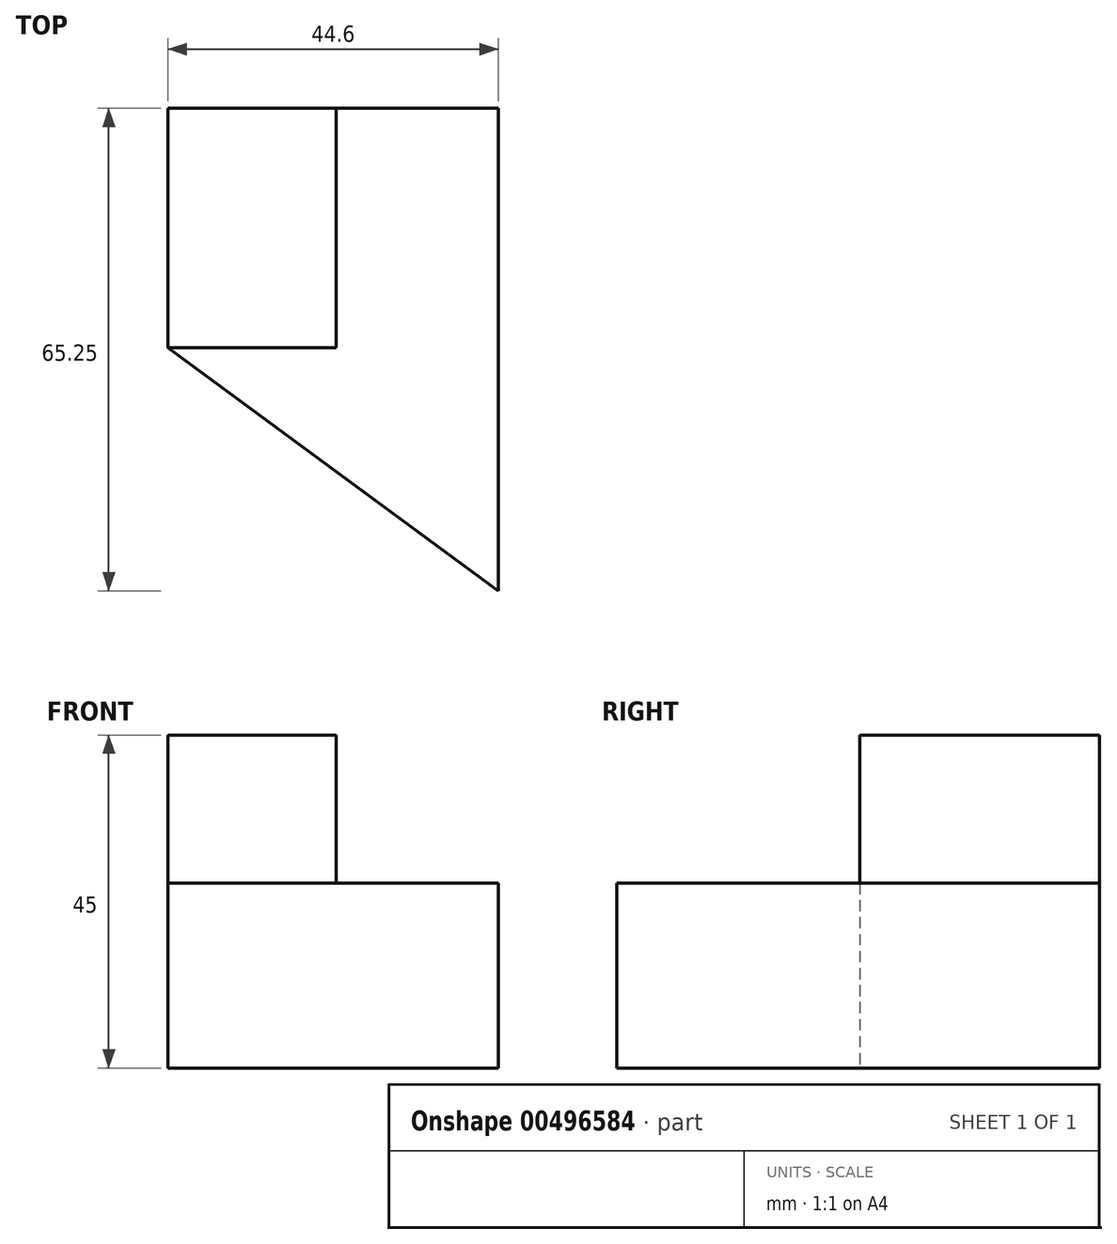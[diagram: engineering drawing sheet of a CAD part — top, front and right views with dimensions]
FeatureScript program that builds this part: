
annotation { "Feature Type Name" : "Feature", "Feature Type Description" : "" }
export const myFeature = defineFeature(function(context is Context, id is Id, definition is map)
    precondition{}
    {
        {
            var Q0;
            Q0=qCreatedBy(makeId("Top.planeOp"),FACE);
            var sketch = newSketch(context, id + "F0", { "sketchPlane" : qUnion([Q0])});
            skLineSegment(sketch, "E0", {"start": v(0, 0) * mm, "end": v(0, 32.37) * mm});
            skLineSegment(sketch, "E1", {"start": v(0, 32.37) * mm, "end": v(44.6, 32.37) * mm});
            skLineSegment(sketch, "E2", {"start": v(44.6, 32.37) * mm, "end": v(44.6, -32.88) * mm});
            skLineSegment(sketch, "E3", {"start": v(44.6, -32.88) * mm, "end": v(0, 0) * mm});
            skSolve(sketch);
        }
        {
            var Q0;
            Q0 = qSketchRegion(id + "F0", true);
            extrude(context, id + "F1", {"entities" : qUnion([Q0]), "depth" : 25 * mm});
        }
        {
            var Q0;
            Q0=makeQuery(id+"F1.opExtrude","CAP_FACE",FACE,{"disambiguationData":[OSD([sQuery(id+"F0.wireOp",EDGE,"E0"),sQuery(id+"F0.wireOp",EDGE,"E1"),sQuery(id+"F0.wireOp",EDGE,"E2"),sQuery(id+"F0.wireOp",EDGE,"E3")])],"isStart":false});
            var sketch = newSketch(context, id + "F2", { "sketchPlane" : qUnion([Q0])});
            skLineSegment(sketch, "E4", {"start": v(0, 0) * mm, "end": v(22.71, 0) * mm});
            skLineSegment(sketch, "E5", {"start": v(22.71, 0) * mm, "end": v(22.71, 32.37) * mm});
            skLineSegment(sketch, "E6", {"start": v(22.71, 32.37) * mm, "end": v(0, 32.37) * mm});
            skSolve(sketch);
        }
        {
            var Q0;
            Q0=makeQuery(id+"F2.imprint","IMPRINT",FACE,{"disambiguationData":[TD([[makeQuery(id+"F2.imprint","IMPRINT",EDGE,{"derivedFrom":sQuery(id+"F2.wireOp",EDGE,"E4")}),1.0]])]});
            extrude(context, id + "F3", {"entities" : qUnion([Q0]), "depth" : 20 * mm});
        }
        {
            var Q0;
            Q0=makeQuery(id+"F1.opExtrude","SWEPT_BODY",BODY,{"disambiguationData":[OSD([sQuery(id+"F0.wireOp",EDGE,"E0"),sQuery(id+"F0.wireOp",EDGE,"E1"),sQuery(id+"F0.wireOp",EDGE,"E2"),sQuery(id+"F0.wireOp",EDGE,"E3")])]});
            transform(context, id + "F4", {"entities" : qUnion([Q0]), "transformType" : TransformType.TRANSLATION_3D, "dx" : 0 * mm, "dy" : 0 * mm, "dz" : 0 * mm, "makeCopy" : true});
        }
    });
